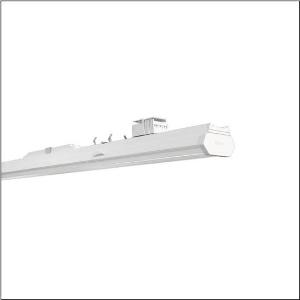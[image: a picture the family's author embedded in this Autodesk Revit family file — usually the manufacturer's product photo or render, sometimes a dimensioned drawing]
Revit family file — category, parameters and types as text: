
# Revit family: licross_r__21_protected_mo_52td12dn4a5g3s_ad63
name_source: partatom
category: Lighting Fixtures
units: mm (PartAtom-declared; Revit-internal decimal feet)

## family parameters
Cut with Voids When Loaded = No
Host = Face
Light Source = No
Part Type = Normal
Room Calculation Point = No
Round Connector Dimension = Use Diameter
Shared = No

## types (1)
- --- (1 x LED, 940 lm, 6.8 W, 4000K)
    Apparent Load = 7 VA
    CIE Flux Codes = 73 92 98 99 100
    Color Rendering = 80
    Color Temperature = 4000K
    Default Elevation = 1800 mm
    Description = Licross® 21 Protected MO, luminaire insert, of sheet steel, galvanised, coil coated, white, length: 1.500mm, width: 90mm, height: 103mm, LED rated luminous flux: 10.700lm, light colour: 840, control gear: DALI 2, with plug, 6-pole, with phase selection, for trunking rail, 14-core, mains connection: 220..240V, AC, 50/60Hz, rated input power: 66W, for trunking rail, 14-core, halogen-free wiring, for emergency light function, converter,control gear: single battery element, battery: LiFeP04, 9Ah, primary light control with lens, of plastic, primary optical cover: cover, of PMMA, light emission: direct distribution, primary light characteristic: symmetric, protection rating (complete): IP54, insulation class (complete): insulation class I (protective earthing), certification: CE, UKCA, protection symbol: D if used in an environment with non-conductive dust loads with corresponding accessories, impact resistance: IK06, permissible ambient temperature for indoor applications: +5..+35°C, standard: EN 60598-2-22, LABS conformity tested according to VDMA 24364:2018-05, reducing of maximum allowable ambient temperature of 5°C with ceiling mounting, corresponds to IFS (International Featured Standards) requirements for safety and quality in the food industry, packaging unit: 1 piece
    Height = 92 mm
    Lamp = 1 x LED
    Lamp Light Flux = 940 lm
    Lamp Power = 6.8 W
    Lamp count = 1
    Length = 1500 mm
    Luminous efficacy = 138 lm/W
    Manufacturer = Siteco
    ModVariant = No
    Model = 52TD12DN4A5G3S
    Mounting Place = Ceiling
    Mounting Type = Pendant
    Number of Poles = 1
    OnlyDefault = Yes
    Power Factor = 1
    Product Name = Licross® 21 Protected MO
    Product group = luminaire insert
    ProductGroupID = 901
    Protection Class = Protection class I
    Protection Degree = IP 54
    RLX_Detail_Level = 1
    RLX_Emergency_Light_Flux = 0 lm
    RLX_Emergency_Type = 0
    RLX_Emergency_Type_DB = No
    RlxData = <blob elided: 24841 chars, md5=010bb7c1>
    Socket = socket
    Standby Power = 0 W
    System Light Flux = 940 lm
    System Power = 7 W
    Type Comments = : emergency light operation: 3 h
    Type Image = l_1256148.jpg
    URL = http://relux.com
    VarID = @adj_059177
    Voltage = 0 V
    Weight = 0.00 kg
    Width = 88 mm

## geometry (parser evidence)
native form markers: Blend x4, Sweep x10
no freeform markers — native parametric forms only
